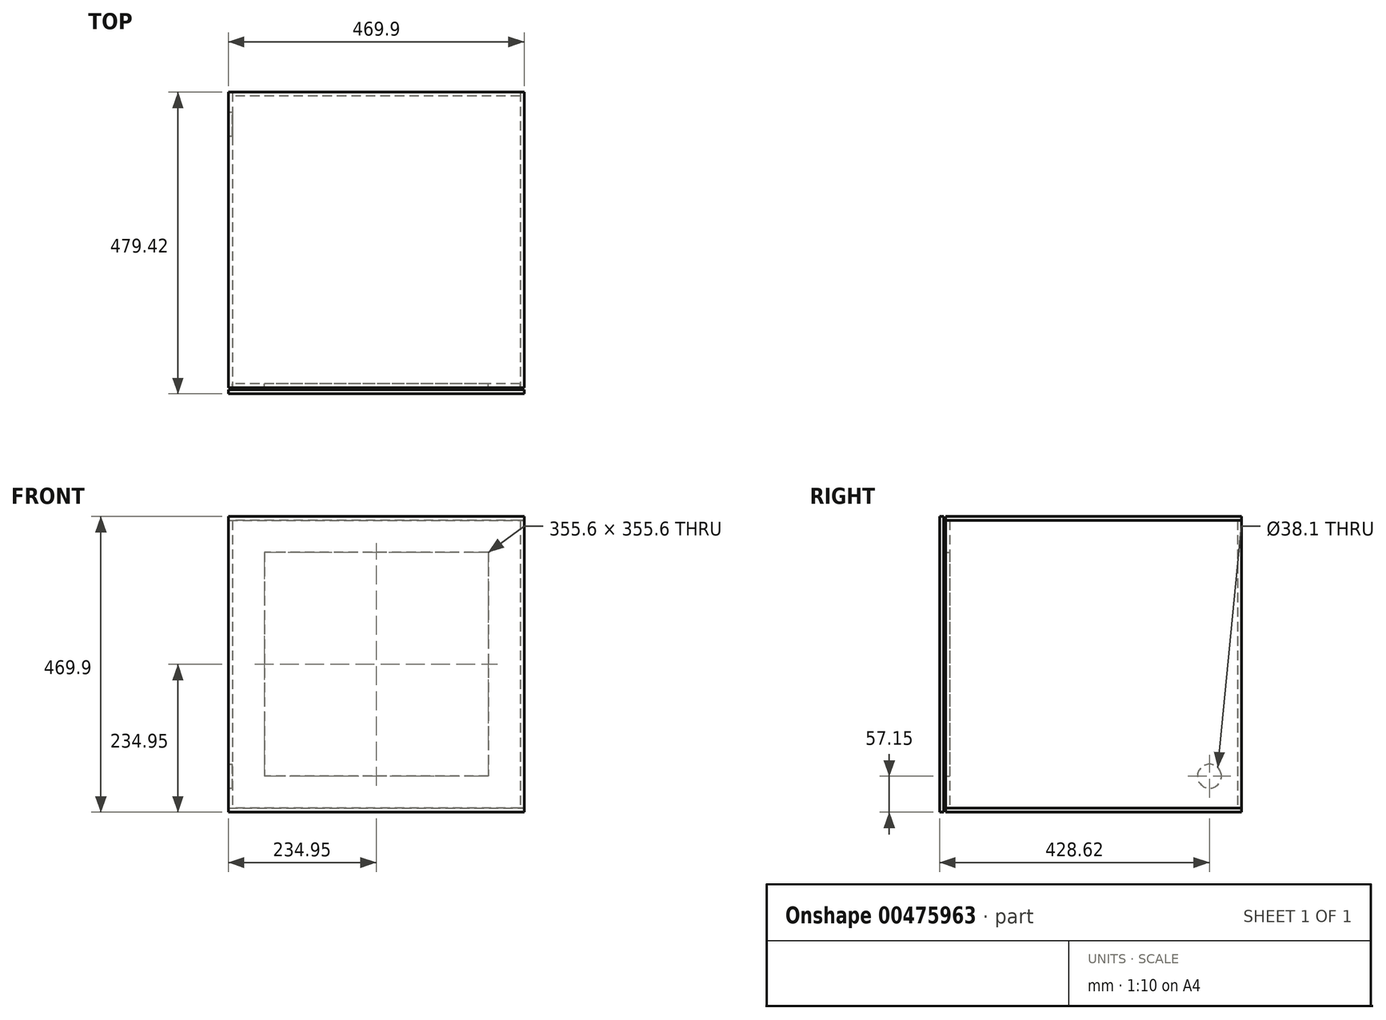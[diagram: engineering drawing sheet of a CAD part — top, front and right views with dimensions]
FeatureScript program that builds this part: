
annotation { "Feature Type Name" : "Feature", "Feature Type Description" : "" }
export const myFeature = defineFeature(function(context is Context, id is Id, definition is map)
    precondition{}
    {
        {
            var Q0;
            Q0=qCreatedBy(makeId("Top.planeOp"),FACE);
            var sketch = newSketch(context, id + "F0", { "sketchPlane" : qUnion([Q0])});
            skLineSegment(sketch, "E0.bottom", {"start": v(-228.6, 228.6) * mm, "end": v(228.6, 228.6) * mm});
            skLineSegment(sketch, "E0.top", {"start": v(-228.6, -228.6) * mm, "end": v(228.6, -228.6) * mm});
            skLineSegment(sketch, "E0.left", {"start": v(-228.6, 228.6) * mm, "end": v(-228.6, -228.6) * mm});
            skLineSegment(sketch, "E0.right", {"start": v(228.6, 228.6) * mm, "end": v(228.6, -228.6) * mm});
            skLineSegment(sketch, "E1", {"start": v(228.6, 0) * mm, "end": v(-228.6, 0) * mm, "construction": true});
            skLineSegment(sketch, "E2", {"start": v(0, -228.6) * mm, "end": v(0, 228.6) * mm, "construction": true});
            skSolve(sketch);
        }
        {
            var Q0;
            Q0=qCreatedBy(makeId("Top.planeOp"),FACE);
            cPlane(context, id + "F1", {"entities" : qUnion([Q0]), "cplaneType" : CPlaneType.OFFSET, "offset" : 228.6 * mm, "width" : 152.4 * mm, "height" : 152.4 * mm});
        }
        {
            var Q0;
            Q0=qCreatedBy(makeId("Top.planeOp"),FACE);
            cPlane(context, id + "F2", {"entities" : qUnion([Q0]), "cplaneType" : CPlaneType.OFFSET, "offset" : 228.6 * mm, "oppositeDirection" : true, "width" : 152.4 * mm, "height" : 152.4 * mm});
        }
        {
            var Q0;
            Q0=qCreatedBy(makeId("Front.planeOp"),FACE);
            cPlane(context, id + "F3", {"entities" : qUnion([Q0]), "cplaneType" : CPlaneType.OFFSET, "offset" : 228.6 * mm, "width" : 152.4 * mm, "height" : 152.4 * mm});
        }
        {
            var Q0;
            Q0=qCreatedBy(makeId("Right.planeOp"),FACE);
            cPlane(context, id + "F4", {"entities" : qUnion([Q0]), "cplaneType" : CPlaneType.OFFSET, "offset" : 228.6 * mm, "oppositeDirection" : true, "width" : 152.4 * mm, "height" : 152.4 * mm});
        }
        {
            var Q0;
            Q0=qCreatedBy(makeId("Front.planeOp"),FACE);
            cPlane(context, id + "F5", {"entities" : qUnion([Q0]), "cplaneType" : CPlaneType.OFFSET, "offset" : 228.6 * mm, "oppositeDirection" : true, "width" : 152.4 * mm, "height" : 152.4 * mm});
        }
        {
            var Q0;
            Q0=qCreatedBy(id+"F2.planeOp",FACE);
            var sketch = newSketch(context, id + "F6", { "sketchPlane" : qUnion([Q0])});
            skLineSegment(sketch, "E3.0", {"start": v(-228.6, 228.6) * mm, "end": v(228.6, 228.6) * mm});
            skLineSegment(sketch, "E4.0", {"start": v(228.6, 228.6) * mm, "end": v(228.6, -228.6) * mm});
            skLineSegment(sketch, "E5.0", {"start": v(-228.6, -228.6) * mm, "end": v(228.6, -228.6) * mm});
            skLineSegment(sketch, "E6.0", {"start": v(-228.6, 228.6) * mm, "end": v(-228.6, -228.6) * mm});
            skLineSegment(sketch, "E7.0", {"start": v(234.95, 234.95) * mm, "end": v(234.95, -234.95) * mm});
            skLineSegment(sketch, "E7.1", {"start": v(-234.95, 234.95) * mm, "end": v(234.95, 234.95) * mm});
            skLineSegment(sketch, "E7.2", {"start": v(-234.95, 234.95) * mm, "end": v(-234.95, -234.95) * mm});
            skLineSegment(sketch, "E7.3", {"start": v(-234.95, -234.95) * mm, "end": v(234.95, -234.95) * mm});
            skSolve(sketch);
        }
        {
            var Q0;
            Q0=qCreatedBy(id+"F1.planeOp",FACE);
            var sketch = newSketch(context, id + "F7", { "sketchPlane" : qUnion([Q0])});
            skLineSegment(sketch, "E8.0", {"start": v(-234.95, 234.95) * mm, "end": v(-234.95, -234.95) * mm});
            skLineSegment(sketch, "E9.0", {"start": v(-234.95, 234.95) * mm, "end": v(234.95, 234.95) * mm});
            skLineSegment(sketch, "E10.0", {"start": v(234.95, 234.95) * mm, "end": v(234.95, -234.95) * mm});
            skLineSegment(sketch, "E11.0", {"start": v(-234.95, -234.95) * mm, "end": v(234.95, -234.95) * mm});
            skSolve(sketch);
        }
        {
            var Q0;
            Q0=qCreatedBy(id+"F4.planeOp",FACE);
            var sketch = newSketch(context, id + "F8", { "sketchPlane" : qUnion([Q0])});
            skPoint(sketch, "E12.0", {"position": v(234.95, 228.6) * mm});
            skPoint(sketch, "E13.0", {"position": v(-234.95, 228.6) * mm});
            skLineSegment(sketch, "E14.bottom", {"start": v(234.95, 228.6) * mm, "end": v(-234.95, 228.6) * mm});
            skLineSegment(sketch, "E14.top", {"start": v(234.95, -228.6) * mm, "end": v(-234.95, -228.6) * mm});
            skLineSegment(sketch, "E14.left", {"start": v(234.95, 228.6) * mm, "end": v(234.95, -228.6) * mm});
            skLineSegment(sketch, "E14.right", {"start": v(-234.95, 228.6) * mm, "end": v(-234.95, -228.6) * mm});
            skCircle(sketch, "E15", {"center": v(184.15, -177.8) * mm, "radius": 19.05 * mm});
            skSolve(sketch);
        }
        {
            var Q0;
            Q0=qCreatedBy(id+"F5.planeOp",FACE);
            var sketch = newSketch(context, id + "F9", { "sketchPlane" : qUnion([Q0])});
            skLineSegment(sketch, "E16.bottom", {"start": v(228.6, 228.6) * mm, "end": v(-228.6, 228.6) * mm});
            skLineSegment(sketch, "E16.top", {"start": v(228.6, -228.6) * mm, "end": v(-228.6, -228.6) * mm});
            skLineSegment(sketch, "E16.left", {"start": v(228.6, 228.6) * mm, "end": v(228.6, -228.6) * mm});
            skLineSegment(sketch, "E16.right", {"start": v(-228.6, 228.6) * mm, "end": v(-228.6, -228.6) * mm});
            skSolve(sketch);
        }
        {
            var Q0;
            Q0=qCreatedBy(id+"F3.planeOp",FACE);
            var sketch = newSketch(context, id + "F10", { "sketchPlane" : qUnion([Q0])});
            skLineSegment(sketch, "E17.0", {"start": v(228.6, 228.6) * mm, "end": v(228.6, -228.6) * mm});
            skLineSegment(sketch, "E18.0", {"start": v(228.6, 228.6) * mm, "end": v(-228.6, 228.6) * mm});
            skLineSegment(sketch, "E19.0", {"start": v(-228.6, 228.6) * mm, "end": v(-228.6, -228.6) * mm});
            skLineSegment(sketch, "E20.0", {"start": v(228.6, -228.6) * mm, "end": v(-228.6, -228.6) * mm});
            skLineSegment(sketch, "E21.0", {"start": v(177.8, 177.8) * mm, "end": v(177.8, -177.8) * mm});
            skLineSegment(sketch, "E21.1", {"start": v(177.8, 177.8) * mm, "end": v(-177.8, 177.8) * mm});
            skLineSegment(sketch, "E21.2", {"start": v(-177.8, 177.8) * mm, "end": v(-177.8, -177.8) * mm});
            skLineSegment(sketch, "E21.3", {"start": v(177.8, -177.8) * mm, "end": v(-177.8, -177.8) * mm});
            skSolve(sketch);
        }
        {
            var Q0;
            Q0=qCreatedBy(id+"F3.planeOp",FACE);
            cPlane(context, id + "F11", {"entities" : qUnion([Q0]), "cplaneType" : CPlaneType.OFFSET, "offset" : 9.52 * mm, "width" : 152.4 * mm, "height" : 152.4 * mm});
        }
        {
            var Q0;
            Q0=qCreatedBy(id+"F11.planeOp",FACE);
            var sketch = newSketch(context, id + "F12", { "sketchPlane" : qUnion([Q0])});
            skLineSegment(sketch, "E22.bottom", {"start": v(-234.95, 234.95) * mm, "end": v(234.95, 234.95) * mm});
            skLineSegment(sketch, "E22.top", {"start": v(-234.95, -234.95) * mm, "end": v(234.95, -234.95) * mm});
            skLineSegment(sketch, "E22.left", {"start": v(-234.95, 234.95) * mm, "end": v(-234.95, -234.95) * mm});
            skLineSegment(sketch, "E22.right", {"start": v(234.95, 234.95) * mm, "end": v(234.95, -234.95) * mm});
            skSolve(sketch);
        }
        {
            var Q0;
            Q0 = qSketchRegion(id + "F12", true);
            extrude(context, id + "F13", {"entities" : qUnion([Q0]), "depth" : 6.35 * mm});
        }
        {
            var Q0;
            Q0=makeQuery(id+"F9.imprint","IMPRINT",FACE,{"disambiguationData":[TD([[makeQuery(id+"F9.imprint","IMPRINT",EDGE,{"derivedFrom":sQuery(id+"F9.wireOp",EDGE,"E16.bottom")}),1.0]])]});
            extrude(context, id + "F14", {"entities" : qUnion([Q0]), "oppositeDirection" : true, "depth" : 6.35 * mm});
        }
        {
            var Q0;
            Q0=makeQuery(id+"F14.opExtrude","SWEPT_BODY",BODY,{"disambiguationData":[OSD([sQuery(id+"F9.wireOp",EDGE,"E16.bottom"),sQuery(id+"F9.wireOp",EDGE,"E16.top"),sQuery(id+"F9.wireOp",EDGE,"E16.left"),sQuery(id+"F9.wireOp",EDGE,"E16.right")])]});
            var Q1;
            Q1=qCreatedBy(makeId("Front.planeOp"),FACE);
            mirror(context, id + "F15", {"entities" : qUnion([Q0]), "mirrorPlane" : qUnion([Q1])});
        }
        {
            var Q0;
            Q0=makeQuery(id+"F10.imprint","IMPRINT",FACE,{"disambiguationData":[TD([[makeQuery(id+"F10.imprint","IMPRINT",EDGE,{"derivedFrom":sQuery(id+"F10.wireOp",EDGE,"E21.0")}),-1.0]])]});
            extrude(context, id + "F16", {"entities" : qUnion([Q0]), "operationType" : NewBodyOperationType.REMOVE, "depth" : 6.35 * mm});
        }
        {
            var Q0;
            Q0 = qSketchRegion(id + "F8", true);
            var Q1;
            Q1=makeQuery(id+"F8.imprint","IMPRINT",FACE,{"disambiguationData":[TD([[makeQuery(id+"F8.imprint","IMPRINT",EDGE,{"derivedFrom":sQuery(id+"F8.wireOp",EDGE,"E15")}),1.0]])]});
            extrude(context, id + "F17", {"entities" : qUnion([Q0, Q1]), "oppositeDirection" : true, "depth" : 6.35 * mm});
        }
        {
            var Q0;
            Q0=makeQuery(id+"F17.opExtrude","SWEPT_BODY",BODY,{"disambiguationData":[OSD([sQuery(id+"F8.wireOp",EDGE,"E14.bottom"),sQuery(id+"F8.wireOp",EDGE,"E14.top"),sQuery(id+"F8.wireOp",EDGE,"E14.left"),sQuery(id+"F8.wireOp",EDGE,"E14.right")])]});
            var Q1;
            Q1=qCreatedBy(makeId("Right.planeOp"),FACE);
            mirror(context, id + "F18", {"entities" : qUnion([Q0]), "mirrorPlane" : qUnion([Q1])});
        }
        {
            var Q0;
            Q0=makeQuery(id+"F8.imprint","IMPRINT",FACE,{"disambiguationData":[TD([[makeQuery(id+"F8.imprint","IMPRINT",EDGE,{"derivedFrom":sQuery(id+"F8.wireOp",EDGE,"E15")}),1.0]])]});
            extrude(context, id + "F19", {"entities" : qUnion([Q0]), "operationType" : NewBodyOperationType.REMOVE, "oppositeDirection" : true, "depth" : 9.52 * mm});
        }
        {
            var Q0;
            Q0 = qSketchRegion(id + "F7", true);
            extrude(context, id + "F20", {"entities" : qUnion([Q0]), "depth" : 6.35 * mm});
        }
        {
            var Q0;
            Q0=makeQuery(id+"F20.opExtrude","SWEPT_BODY",BODY,{"disambiguationData":[OSD([sQuery(id+"F7.wireOp",EDGE,"E8.0"),sQuery(id+"F7.wireOp",EDGE,"E9.0"),sQuery(id+"F7.wireOp",EDGE,"E10.0"),sQuery(id+"F7.wireOp",EDGE,"E11.0")])]});
            var Q1;
            Q1=qCreatedBy(makeId("Top.planeOp"),FACE);
            mirror(context, id + "F21", {"entities" : qUnion([Q0]), "mirrorPlane" : qUnion([Q1])});
        }
    });
